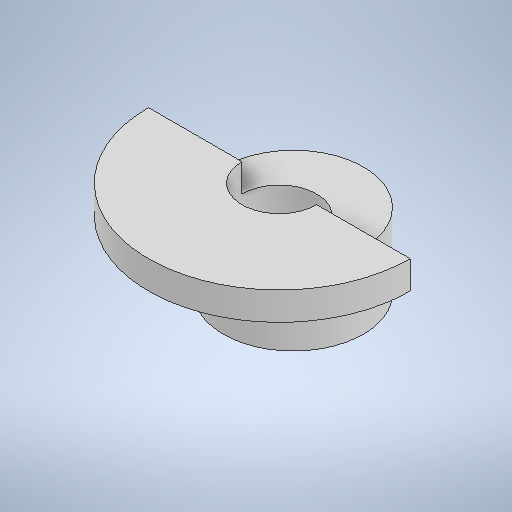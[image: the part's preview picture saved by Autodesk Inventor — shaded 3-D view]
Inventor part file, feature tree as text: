
AUTODESK INVENTOR PART (.ipt)
format: ipt  version: 2025.1 (Build 291241000, 241)  size: 273,920 bytes
history: native  units: mm
features: sketch x4, extrude x2, hole x2, plane x2, mirror x1, projected_geometry x1
ambient origin geometry x8: Origin, YZ Plane, XZ Plane, XY Plane, X Axis, Y Axis, Z Axis, Center Point
bodies: Solid1 (feature_tree)
feature tree (12):
  extrude  "Extrusion1"  Depth=3.0mm TaperAngle=0.0deg
  extrude  "Extrusion2"  Depth=9.0mm
  hole  "Hole1"  [1 undecoded]
  plane  "Work Plane1"
  hole  "Hole2"  [1 undecoded]
  plane  "Work Plane2"
  mirror  "Mirror1"
  sketch  "Sketch1"  dims[d0=28.0mm d1=3.0mm d2=0.0mm]
  sketch  "Sketch2"  dims[d4=8.0mm d5=0.0mm]
  sketch  "Sketch3"  dims[d6=8.0mm d7=6.0mm d8=4.0mm d9=2.0mm d10=90.0deg d11=8.0mm d12=0.0mm d13=9.0mm]
  sketch  "Sketch4"  dims[d15=2.459mm d16=3.5mm d17=4.0mm d18=2.0mm d19=90.0deg d20=3.5mm d21=0.0mm d22=15.0mm d23=1.5mm d24=0.0mm]
  projected_geometry  "Projected Loop1"
note: 2 required parameter values undecoded (feature->parameter linkage not recoverable at this tier; creation-order binding heuristic only, values carry confidence <= 0.55)
